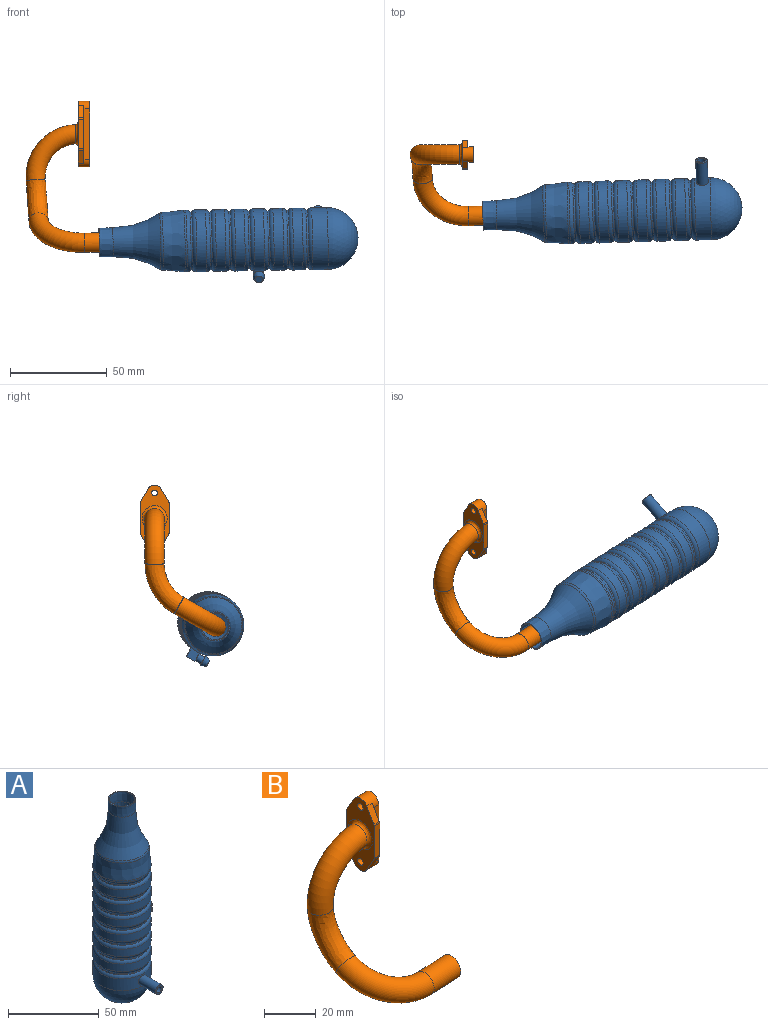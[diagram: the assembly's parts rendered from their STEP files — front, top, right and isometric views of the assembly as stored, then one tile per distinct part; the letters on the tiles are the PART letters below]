
ASSEMBLY  parts=2 mates=1
PART A: 81 faces, bbox 39.8x47.3x135 mm
  f0: torus R=13.5mm, axis (0,0,1), area 228mm2, adj f5,f18,f73,f74,f75
  f1: cylinder r=16mm len=32mm, axis (0,0,-1), area 775.6mm2, adj f8,f10,f69
  f2: cylinder r=16mm len=32mm, axis (0,0,-1), area 502.7mm2, adj f25,f28
  f3: cylinder r=16mm len=32mm, axis (0,0,-1), area 502.7mm2, adj f22,f24
  f4: cylinder r=16mm len=32mm, axis (0,0,-1), area 502.7mm2, adj f19,f21
  f5: cylinder r=16mm len=32mm, axis (0,0,-1), area 477.6mm2, adj f0,f17,f72,f73,f75
  f6: cylinder r=16mm len=32mm, axis (0,0,-1), area 502.7mm2, adj f14,f16
  f7: cylinder r=16mm len=32mm, axis (0,0,-1), area 502.7mm2, adj f11,f13
  f8: sphere r=16mm, area 1608.5mm2, adj f1
  f9: cylinder r=15mm len=30mm, axis (0,0,1), area 94.2mm2, adj f10,f11
  f10: torus R=13.5mm, axis (0,0,1), area 228.1mm2, adj f1,f9
  f11: torus R=13.5mm, axis (0,0,-1), area 228.1mm2, adj f7,f9
  f12: cylinder r=15mm len=30mm, axis (0,0,1), area 94.2mm2, adj f13,f14
  f13: torus R=13.5mm, axis (0,0,1), area 228.1mm2, adj f7,f12
  f14: torus R=13.5mm, axis (0,0,-1), area 228.1mm2, adj f6,f12
  f15: cylinder r=15mm len=30mm, axis (0,0,1), area 94.2mm2, adj f16,f17
  f16: torus R=13.5mm, axis (0,0,1), area 228.1mm2, adj f6,f15
  f17: torus R=13.5mm, axis (0,0,-1), area 228.1mm2, adj f5,f15
  f18: cylinder r=15mm len=30mm, axis (0,0,1), area 94.2mm2, adj f0,f19
  f19: torus R=13.5mm, axis (0,0,-1), area 228.1mm2, adj f4,f18
  f20: cylinder r=15mm len=30mm, axis (0,0,1), area 94.2mm2, adj f21,f22
  f21: torus R=13.5mm, axis (0,0,1), area 228.1mm2, adj f4,f20
  f22: torus R=13.5mm, axis (0,0,-1), area 228.1mm2, adj f3,f20
  f23: cylinder r=15mm len=30mm, axis (0,0,1), area 94.2mm2, adj f24,f25
  f24: torus R=13.5mm, axis (0,0,1), area 228.1mm2, adj f3,f23
  f25: torus R=13.5mm, axis (0,0,-1), area 228.1mm2, adj f2,f23
  f26: cylinder r=15mm len=30mm, axis (0,0,1), area 94.2mm2, adj f28,f29
  f27: cylinder r=16mm len=32mm, axis (0,0,-1), area 100.5mm2, adj f29,f30
  f28: torus R=13.5mm, axis (0,0,1), area 228.1mm2, adj f2,f26
  f29: torus R=13.5mm, axis (0,0,-1), area 228.1mm2, adj f26,f27
  f30: bspline ~32x32mm, area 1107.1mm2, adj f27,f32
  f31: bspline ~30x30mm, area 1595.7mm2, adj f32,f33
  f32: bspline ~30.02x30.01mm, area 123.6mm2, adj f30,f31
  f33: extruded ~15x15mm, area 329.9mm2, adj f31,f34
  f34: plane 15.02x15.02mm, normal (0,0,1), area 22.8mm2, adj f33,f68
  f35: cylinder r=15.5mm len=31mm, axis (0,0,-1), area 486.9mm2, adj f60,f63
  f36: cylinder r=15.5mm len=31mm, axis (0,0,-1), area 486.9mm2, adj f57,f59
  f37: cylinder r=15.5mm len=31mm, axis (0,0,-1), area 486.9mm2, adj f54,f56
  f38: cylinder r=15.5mm len=31mm, axis (0,0,-1), area 486.9mm2, adj f51,f53
  f39: cylinder r=15.5mm len=31mm, axis (0,0,-1), area 486.9mm2, adj f48,f50
  f40: cylinder r=15.5mm len=31mm, axis (0,0,-1), area 486.9mm2, adj f45,f47
  f41: cylinder r=15.5mm len=31mm, axis (0,0,-1), area 766.6mm2, adj f42,f44,f71
  f42: sphere r=15.5mm, area 1509.5mm2, adj f41
  f43: cylinder r=14.5mm len=29mm, axis (0,0,1), area 139.9mm2, adj f44,f45
  f44: torus R=13.5mm, axis (0,0,1), area 199.4mm2, adj f41,f43
  f45: torus R=13.5mm, axis (0,0,-1), area 199.4mm2, adj f40,f43
  f46: cylinder r=14.5mm len=29mm, axis (0,0,1), area 139.9mm2, adj f47,f48
  f47: torus R=13.5mm, axis (0,0,1), area 199.4mm2, adj f40,f46
  f48: torus R=13.5mm, axis (0,0,-1), area 199.4mm2, adj f39,f46
  f49: cylinder r=14.5mm len=29mm, axis (0,0,1), area 139.9mm2, adj f50,f51
  f50: torus R=13.5mm, axis (0,0,1), area 199.4mm2, adj f39,f49
  f51: torus R=13.5mm, axis (0,0,-1), area 199.4mm2, adj f38,f49
  f52: cylinder r=14.5mm len=29mm, axis (0,0,1), area 139.9mm2, adj f53,f54
  f53: torus R=13.5mm, axis (0,0,1), area 199.4mm2, adj f38,f52
  f54: torus R=13.5mm, axis (0,0,-1), area 199.4mm2, adj f37,f52
  f55: cylinder r=14.5mm len=29mm, axis (0,0,1), area 139.9mm2, adj f56,f57
  f56: torus R=13.5mm, axis (0,0,1), area 199.4mm2, adj f37,f55
  f57: torus R=13.5mm, axis (0,0,-1), area 199.4mm2, adj f36,f55
  f58: cylinder r=14.5mm len=29mm, axis (0,0,1), area 139.9mm2, adj f59,f60
  f59: torus R=13.5mm, axis (0,0,1), area 199.4mm2, adj f36,f58
  f60: torus R=13.5mm, axis (0,0,-1), area 199.4mm2, adj f35,f58
  f61: cylinder r=14.5mm len=29mm, axis (0,0,1), area 139.9mm2, adj f63,f64
  f62: cylinder r=15.5mm len=31mm, axis (0,0,-1), area 97.4mm2, adj f64,f65
  f63: torus R=13.5mm, axis (0,0,1), area 199.4mm2, adj f35,f61
  f64: torus R=13.5mm, axis (0,0,-1), area 199.4mm2, adj f61,f62
  f65: offset ~33x33mm, area 1070.6mm2, adj f62,f67
  f66: offset ~31x31mm, area 1534.8mm2, adj f67,f68
  f67: bspline ~29.02x29.01mm, area 95.7mm2, adj f65,f66
  f68: extruded ~14x14mm, area 307.9mm2, adj f34,f66
  f69: cylinder r=3mm len=13mm, axis (0,1,0), area 245mm2, adj f1,f70
  f70: plane 6x6mm, normal (0,-1,0), area 15.7mm2, adj f69,f71
  f71: cylinder r=2mm len=13.5mm, axis (0,-1,0), area 169.6mm2, adj f41,f70
  f72: plane 5.2x5mm, normal (0,0,-1), area 25.3mm2, adj f5,f73,f75,f76
  f73: plane 5.2x5mm, normal (0,1,0), area 13.4mm2, adj f0,f5,f72,f74,f76,f77
  f74: plane 5.2x5mm, normal (0,0,1), area 25.3mm2, adj f0,f73,f75,f76
  f75: plane 5.2x5mm, normal (0,-1,0), area 26mm2, adj f0,f5,f72,f74,f76
  f76: plane 5x5mm, normal (1,0,0), area 25mm2, adj f72,f73,f74,f75
  f77: cylinder r=2mm len=4mm, axis (0,-1,0), area 44mm2, adj f73,f78
  f78: plane 6x6mm, normal (0,-1,0), area 15.7mm2, adj f77,f79
  f79: cone r=3mm half-angle=18.4deg, axis (0,-1,0), area 49.7mm2, adj f78,f80
  f80: plane 4x4mm, normal (0,1,0), area 12.6mm2, adj f79
PART B: 40 faces, bbox 47.7x48.5x79.2 mm
  f0: plane 4x0.47mm, normal (-1,0,0), area 1.3mm2, adj f24,f31
  f1: plane 8.06x2.5mm, normal (-1,0,0), area 14.4mm2, adj f23,f24
  f2: plane 4x0.47mm, normal (-1,0,0), area 1.3mm2, adj f24,f32
  f3: plane 8.06x2.5mm, normal (-1,0,0), area 14.4mm2, adj f21,f24
  f4: plane 34x8mm, normal (1,0,0), area 164.1mm2, adj f8,f14,f16,f17,f18,f19,f20,f21
  f5: plane 30x4.03mm, normal (1,0,0), area 77.4mm2, adj f6,f7,f8,f13,f14,f17,f27,f29
  f6: plane 15.2x3mm, normal (0,1,0), area 45.6mm2, adj f5,f12,f27,f29
  f7: plane 6.65x3.83mm, normal (0,0.87,0.5), area 23mm2, adj f5,f8,f12,f29
  f8: cylinder r=4mm len=8mm, axis (-1,0,0), area 62.8mm2, adj f4,f5,f7,f9,f11,f12,f16,f17
  f9: plane 6.65x3.83mm, normal (0,-0.87,0.5), area 23mm2, adj f8,f11,f12,f30
  f10: plane 15.2x3mm, normal (0,-1,0), area 45.6mm2, adj f11,f12,f28,f30
  f11: plane 30x4.03mm, normal (1,0,0), area 77.4mm2, adj f8,f9,f10,f14,f15,f16,f28,f30
  f12: plane 34x15mm, normal (-1,0,0), area 265.9mm2, adj f6,f7,f8,f9,f10,f13,f14,f15
  f13: plane 6.65x3.83mm, normal (0,0.87,-0.5), area 23mm2, adj f5,f12,f14,f27
  f14: cylinder r=4mm len=8mm, axis (-1,0,0), area 62.8mm2, adj f4,f5,f11,f12,f13,f15,f16,f17
  f15: plane 6.65x3.83mm, normal (0,-0.87,-0.5), area 23mm2, adj f11,f12,f14,f28
  f16: plane 26x3mm, normal (0,-1,0), area 78mm2, adj f4,f8,f11,f14
  f17: plane 26x3mm, normal (0,1,0), area 78mm2, adj f4,f5,f8,f14
  f18: cylinder r=1.5mm len=6mm, axis (1,0,0), area 56.5mm2, adj f4,f12
  f19: cylinder r=1.5mm len=6mm, axis (1,0,0), area 56.5mm2, adj f4,f12
  f20: plane 4x3mm, normal (0,0,1), area 12mm2, adj f4,f21,f23,f31
  f21: plane 20x6mm, normal (0,-1,0), area 102.1mm2, adj f3,f4,f20,f22,f31,f32
  f22: plane 4x3mm, normal (0,0,-1), area 12mm2, adj f4,f21,f23,f32
  f23: plane 20x6mm, normal (0,1,0), area 102.1mm2, adj f1,f4,f20,f22,f31,f32
  f24: torus R=22mm, axis (0,-1,0), area 1020.5mm2, adj f0,f1,f2,f3,f34
  f25: torus R=22mm, axis (0,-1,0), area 1086.2mm2, adj f26,f33
  f26: bspline ~13.04x13.01mm, area 82.7mm2, adj f12,f25
  f27: cylinder r=1.5mm len=3mm, axis (-1,0,0), area 2.4mm2, adj f5,f6,f12,f13
  f28: cylinder r=1.5mm len=3mm, axis (-1,0,0), area 2.4mm2, adj f10,f11,f12,f15
  f29: cylinder r=1.5mm len=3mm, axis (-1,0,0), area 2.4mm2, adj f5,f6,f7,f12
  f30: cylinder r=1.5mm len=3mm, axis (-1,0,0), area 2.4mm2, adj f9,f10,f11,f12
  f31: plane 5.97x4mm, normal (0.89,0,0.45), area 26.7mm2, adj f0,f20,f21,f23
  f32: plane 5.97x4mm, normal (0.89,0,-0.45), area 26.7mm2, adj f2,f21,f22,f23
  f33: bspline ~30.93x27.5mm, area 824.1mm2, adj f25,f35
  f34: bspline ~30x26mm, area 741.6mm2, adj f24,f36
  f35: torus R=23mm, axis (0,0.5,-0.87), area 1135mm2, adj f33,f37
  f36: torus R=23mm, axis (0,0.5,-0.87), area 1021.5mm2, adj f34,f38
  f37: cylinder r=5mm len=15.34mm, axis (-1,-0.03,-0.02), area 471.2mm2, adj f35,f39
  f38: cylinder r=4.5mm len=15.3mm, axis (-1,-0.03,-0.02), area 424.1mm2, adj f36,f39
  f39: plane 10x10mm, normal (1,0.03,0.02), area 14.9mm2, adj f37,f38
PLACE A rot(axis=(-0.7,-0.2,0.69),160.3deg) t=(49.81,-28.27,-2.08)mm
PLACE B rot(axis=(1,0.03,0.02),0deg) t=(-78.97,-0.34,51.94)mm
MATE slider B.f37 <-> A.f1  axis (-1,-0.03,-0.02) through (-68.12,-31.84,-4.13)mm
